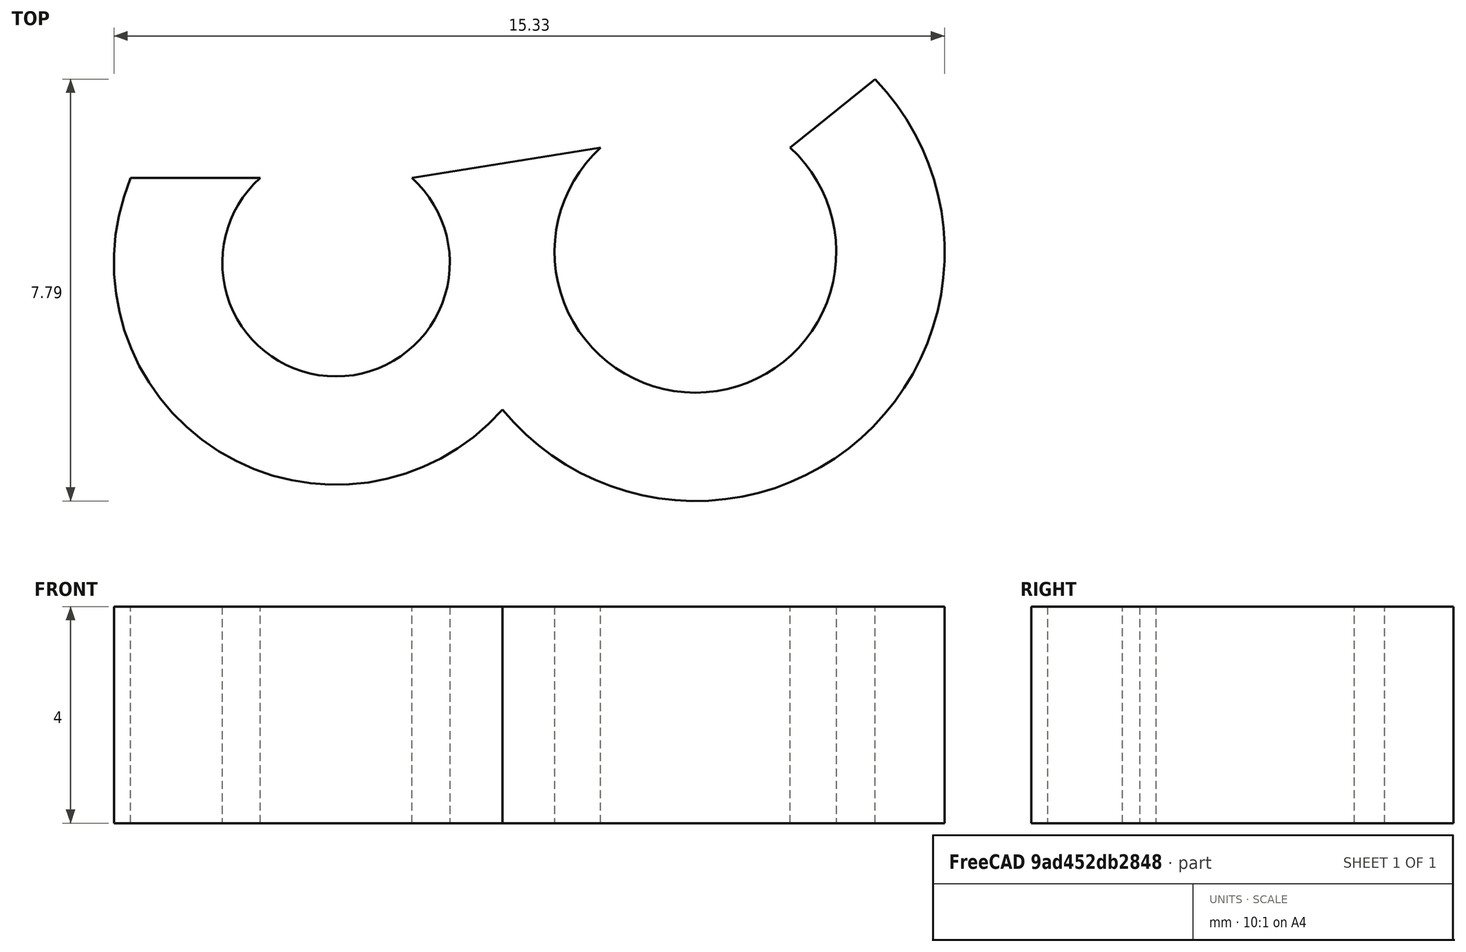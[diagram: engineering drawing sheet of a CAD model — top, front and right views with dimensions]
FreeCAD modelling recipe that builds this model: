
FCSTD DOCUMENT  (FreeCAD 0.17R13519 (Git))
Label: QiGan-jwei-1.0
License: All rights reserved
LicenseURL: http://en.wikipedia.org/wiki/All_rights_reserved
objects: Sketcher::SketchObject×1, PartDesign::Pad×1, PartDesign::Body×1
note: 4 computed .brp shape members not serialized (recipe doc carries the construction recipe); baked Part::Feature solids carry a one-line shape summary decoded from their .brp

FEATURE [Sketcher::SketchObject] Sketch
  MapMode = 5
  Support = -> [XY_Plane]
  sketch-geometry (7):
    g0: ArcOfCircle CenterX=0 CenterY=1 CenterZ=0 NormalX=0 NormalY=0 NormalZ=1 AngleXU=0 Radius=2.1 StartAngle=2.30052 EndAngle=7.12425
    g1: ArcOfCircle CenterX=6.63325 CenterY=1.2 CenterZ=0 NormalX=0 NormalY=0 NormalZ=1 AngleXU=0 Radius=2.6 StartAngle=2.30916 EndAngle=7.11562
    g2: ArcOfCircle CenterX=6.63325 CenterY=1.2 CenterZ=0 NormalX=0 NormalY=0 NormalZ=1 AngleXU=0 Radius=4.6 StartAngle=3.8275 EndAngle=7.04979
    g3: ArcOfCircle CenterX=0 CenterY=1 CenterZ=0 NormalX=0 NormalY=0 NormalZ=1 AngleXU=0 Radius=4.1 StartAngle=2.74988 EndAngle=5.55992
    g4: LineSegment StartX=-3.78946 StartY=2.56525 StartZ=0 EndX=-1.4 EndY=2.56525 EndZ=0
    g5: LineSegment StartX=1.4 StartY=2.56525 StartZ=0 EndX=4.88325 EndY=3.12289 EndZ=0
    g6: LineSegment StartX=8.38325 StartY=3.12289 StartZ=0 EndX=9.94651 EndY=4.39098 EndZ=0
  constraints (21):
    c: Radius(g0) = 2.1
    c: Distance(g0,g0) = 2.8
    c: Radius(g1) = 2.6
    c: Distance(g1,g1) = 3.5
    c: DistanceY(g-1,g1) = 1.2
    c: Coincident(g2,g1)
    c: Radius(g2) = 4.6
    c: Horizontal(g0,g0)
    c: Radius(g3) = 4.1
    c: Horizontal(g1,g1)
    c: Coincident(g3,g0)
    c: PointOnObject(g0,g-2)
    c: Distance(g-1,g0) = 1
    c: PointOnObject(g2,g3)
    c: Coincident(g3,g2)
    c: Coincident(g4,g3)
    c: Coincident(g4,g0)
    c: Coincident(g5,g0)
    c: Coincident(g5,g1)
    c: Coincident(g6,g1)
    c: Coincident(g6,g2)
FEATURE [PartDesign::Pad] Pad
  Length = 4
  Length2 = 100
  Profile = -> Sketch
  Type = 0
FEATURE [PartDesign::Body] Body
  Group = -> [Sketch,Pad]
  Origin = -> Origin
  Tip = -> Pad
